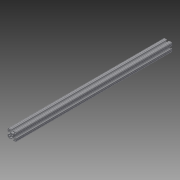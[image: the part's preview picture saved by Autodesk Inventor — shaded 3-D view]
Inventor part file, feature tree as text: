
AUTODESK INVENTOR PART (.ipt)
format: ipt  version: 2013 (Build 170138000, 138)  size: 293,888 bytes
history: native  units: in
note: dims shown in document units (in); Inventor stores cm internally (conversion verified against a paired STEP export)
features: extrude x1, sketch x1
ambient origin geometry x8: Origin, YZ Plane, XZ Plane, XY Plane, X Axis, Y Axis, Z Axis, Center Point
bodies: Solid1 (feature_tree)
feature tree (2):
  extrude  "Extrusion1"  [1 undecoded]
  sketch  "Sketch1"  dims[d0=28.0in d1=0.0in]
note: 1 required parameter value undecoded (feature->parameter linkage not recoverable at this tier; creation-order binding heuristic only, values carry confidence <= 0.55)
